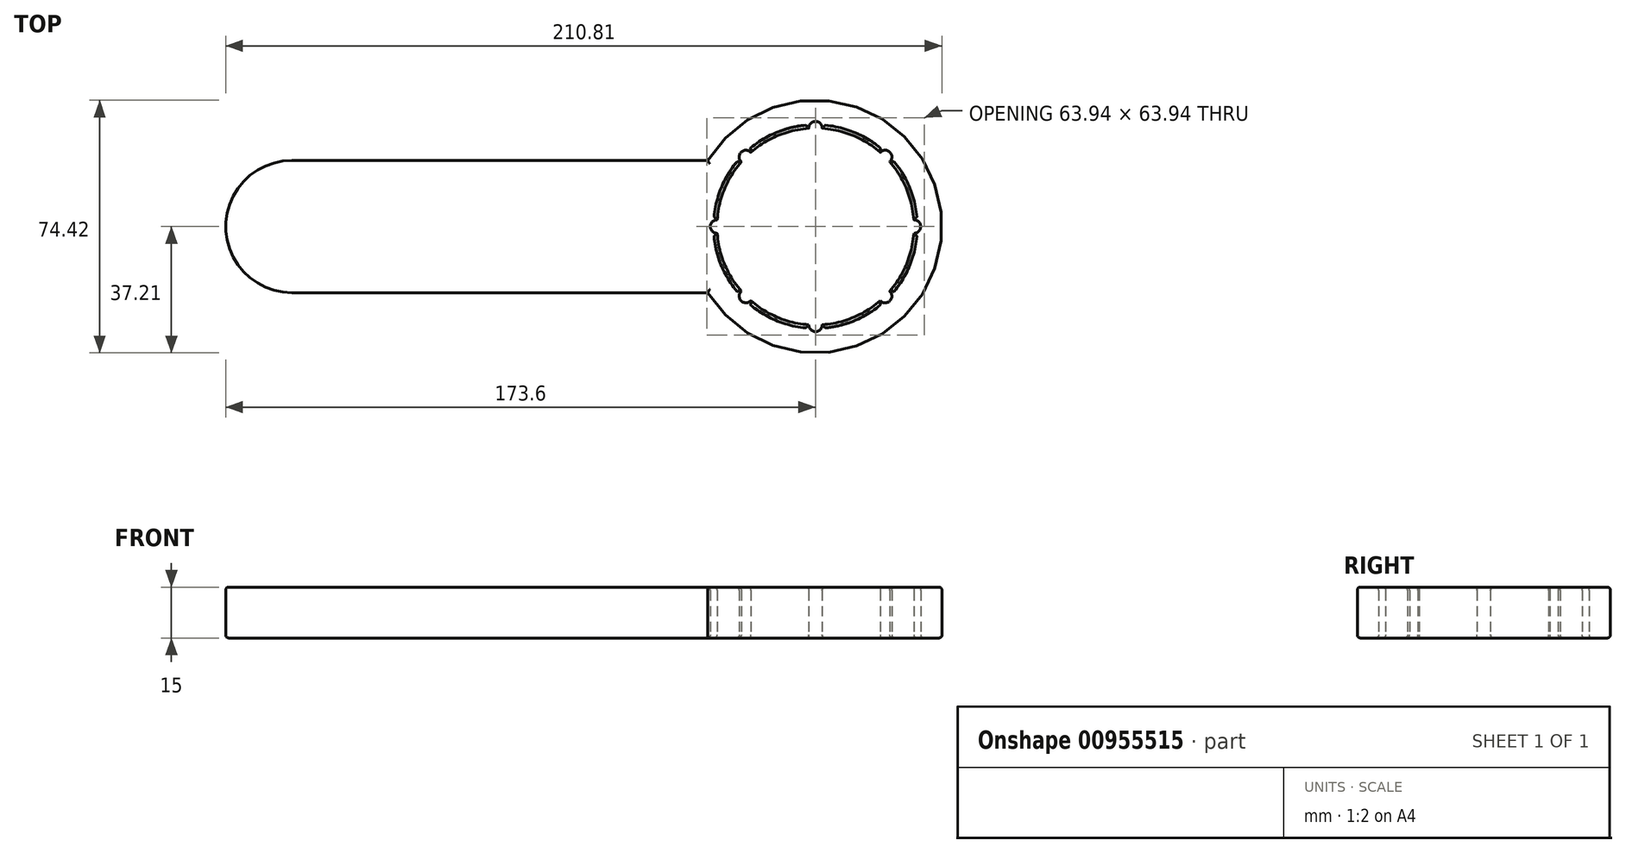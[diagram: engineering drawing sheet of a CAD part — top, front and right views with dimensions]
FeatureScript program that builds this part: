
annotation { "Feature Type Name" : "Feature", "Feature Type Description" : "" }
export const myFeature = defineFeature(function(context is Context, id is Id, definition is map)
    precondition{}
    {
        {
            var Q0;
            Q0=qCreatedBy(makeId("Top.planeOp"),FACE);
            var sketch = newSketch(context, id + "F0", { "sketchPlane" : qUnion([Q0])});
            skCircle(sketch, "E0", {"center": v(0, 0) * mm, "radius": 37.21 * mm});
            skArc(sketch, "E1", {"start": v(-20.5, 20.5) * mm, "mid": v(-26.4, 12) * mm, "end": v(-28.93, 1.95) * mm});
            skPoint(sketch, "E2", {"position": v(0, 29) * mm});
            skPoint(sketch, "E3", {"position": v(0, -29) * mm});
            skLineSegment(sketch, "E4.bottom", {"start": v(-31.72, 19.47) * mm, "end": v(-154.13, 19.47) * mm});
            skLineSegment(sketch, "E4.top", {"start": v(-3.98, -19.47) * mm, "end": v(-154.13, -19.47) * mm});
            skLineSegment(sketch, "E4.left", {"start": v(-3.98, 19.47) * mm, "end": v(-3.98, -19.47) * mm});
            skLineSegment(sketch, "E4.right", {"start": v(-154.13, 19.47) * mm, "end": v(-154.13, -19.47) * mm});
            skArc(sketch, "E5", {"start": v(-154.13, 19.47) * mm, "mid": v(-173.6, 0) * mm, "end": v(-154.13, -19.47) * mm});
            skArc(sketch, "E6.trimOffspring", {"start": v(-29, 0) * mm, "mid": v(-27.15, -10.2) * mm, "end": v(-21.84, -19.08) * mm});
            skArc(sketch, "E7.trimOffspring", {"start": v(-20.5, -20.5) * mm, "mid": v(-12, -26.4) * mm, "end": v(-1.95, -28.93) * mm});
            skArc(sketch, "E8.trimOffspring", {"start": v(0, -29) * mm, "mid": v(10.2, -27.15) * mm, "end": v(19.08, -21.84) * mm});
            skArc(sketch, "E9.trimOffspring", {"start": v(20.5, -20.5) * mm, "mid": v(26.4, -12) * mm, "end": v(28.93, -1.95) * mm});
            skArc(sketch, "E10.trimOffspring", {"start": v(20.5, 20.5) * mm, "mid": v(12, 26.4) * mm, "end": v(1.95, 28.93) * mm});
            skArc(sketch, "E11.trimOffspring", {"start": v(0, 29) * mm, "mid": v(-10.2, 27.15) * mm, "end": v(-19.08, 21.84) * mm});
            skPoint(sketch, "E12", {"position": v(-1.95, 29) * mm});
            skPoint(sketch, "E13", {"position": v(-21.88, 19.13) * mm});
            skPoint(sketch, "E14", {"position": v(-29, -1.95) * mm});
            skPoint(sketch, "E15", {"position": v(-19.13, -21.88) * mm});
            skPoint(sketch, "E16", {"position": v(1.95, -29) * mm});
            skPoint(sketch, "E17", {"position": v(21.88, -19.13) * mm});
            skPoint(sketch, "E18", {"position": v(29, 1.95) * mm});
            skPoint(sketch, "E19", {"position": v(19.13, 21.88) * mm});
            skCircle(sketch, "E20", {"center": v(0, 29) * mm, "radius": 1.97 * mm});
            skCircle(sketch, "E21.1.0", {"center": v(-20.5, 20.5) * mm, "radius": 1.97 * mm});
            skCircle(sketch, "E21.2.0", {"center": v(-29, 0) * mm, "radius": 1.97 * mm});
            skCircle(sketch, "E22.1.3.0", {"center": v(-20.5, -20.5) * mm, "radius": 1.97 * mm});
            skCircle(sketch, "E22.1.4.0", {"center": v(0, -29) * mm, "radius": 1.97 * mm});
            skCircle(sketch, "E22.1.5.0", {"center": v(20.5, -20.5) * mm, "radius": 1.97 * mm});
            skCircle(sketch, "E22.1.6.0", {"center": v(29, 0) * mm, "radius": 1.97 * mm});
            skCircle(sketch, "E22.1.7.0", {"center": v(20.5, 20.5) * mm, "radius": 1.97 * mm});
            skArc(sketch, "E22.2.7.0", {"start": v(29, 0) * mm, "mid": v(27.15, 10.2) * mm, "end": v(21.84, 19.08) * mm});
            skSolve(sketch);
        }
        {
            var Q0;
            Q0 = qSketchRegion(id + "F0", true);
            extrude(context, id + "F1", {"entities" : qUnion([Q0]), "depth" : 15 * mm, "offsetDistance" : 25 * mm});
        }
        {
            var Q0;
            Q0=makeQuery(id+"F1.opExtrude","CAP_FACE",FACE,{"disambiguationData":[OSD([sQuery(id+"F0.wireOp",EDGE,"E0"),sQuery(id+"F0.wireOp",EDGE,"E4.bottom"),sQuery(id+"F0.wireOp",EDGE,"E4.top"),sQuery(id+"F0.wireOp",EDGE,"E4.left"),sQuery(id+"F0.wireOp",EDGE,"E5"),sQuery(id+"F0.wireOp",EDGE,"E10.trimOffspring"),sQuery(id+"F0.wireOp",EDGE,"E20"),sQuery(id+"F0.wireOp",EDGE,"E21.1.0"),sQuery(id+"F0.wireOp",EDGE,"E11.trimOffspring"),sQuery(id+"F0.wireOp",EDGE,"E21.2.0"),sQuery(id+"F0.wireOp",EDGE,"E1"),sQuery(id+"F0.wireOp",EDGE,"E22.1.3.0"),sQuery(id+"F0.wireOp",EDGE,"E6.trimOffspring"),sQuery(id+"F0.wireOp",EDGE,"E22.1.4.0"),sQuery(id+"F0.wireOp",EDGE,"E7.trimOffspring"),sQuery(id+"F0.wireOp",EDGE,"E22.1.5.0"),sQuery(id+"F0.wireOp",EDGE,"E8.trimOffspring"),sQuery(id+"F0.wireOp",EDGE,"E22.1.6.0"),sQuery(id+"F0.wireOp",EDGE,"E9.trimOffspring"),sQuery(id+"F0.wireOp",EDGE,"E22.1.7.0"),sQuery(id+"F0.wireOp",EDGE,"E22.2.7.0")])],"isStart":false});
            fillet(context, id + "F2", {"entities" : qUnion([Q0]), "radius" : 1 * mm, "tangentPropagation" : true, "rho" : 0.5, "crossSection" : FilletCrossSection.CONIC, "allowEdgeOverflow" : false});
        }
        {
            var Q0;
            Q0=makeQuery(id+"F1.opExtrude","CAP_FACE",FACE,{"disambiguationData":[OSD([sQuery(id+"F0.wireOp",EDGE,"E0"),sQuery(id+"F0.wireOp",EDGE,"E4.bottom"),sQuery(id+"F0.wireOp",EDGE,"E4.top"),sQuery(id+"F0.wireOp",EDGE,"E5"),sQuery(id+"F0.wireOp",EDGE,"E10.trimOffspring"),sQuery(id+"F0.wireOp",EDGE,"E20"),sQuery(id+"F0.wireOp",EDGE,"E21.1.0"),sQuery(id+"F0.wireOp",EDGE,"E11.trimOffspring"),sQuery(id+"F0.wireOp",EDGE,"E21.2.0"),sQuery(id+"F0.wireOp",EDGE,"E1"),sQuery(id+"F0.wireOp",EDGE,"E22.1.3.0"),sQuery(id+"F0.wireOp",EDGE,"E6.trimOffspring"),sQuery(id+"F0.wireOp",EDGE,"E22.1.4.0"),sQuery(id+"F0.wireOp",EDGE,"E7.trimOffspring"),sQuery(id+"F0.wireOp",EDGE,"E22.1.5.0"),sQuery(id+"F0.wireOp",EDGE,"E8.trimOffspring"),sQuery(id+"F0.wireOp",EDGE,"E22.1.6.0"),sQuery(id+"F0.wireOp",EDGE,"E9.trimOffspring"),sQuery(id+"F0.wireOp",EDGE,"E22.1.7.0"),sQuery(id+"F0.wireOp",EDGE,"E22.2.7.0")])],"isStart":true});
            fillet(context, id + "F3", {"entities" : qUnion([Q0]), "radius" : 1 * mm, "tangentPropagation" : true, "rho" : 0.5, "crossSection" : FilletCrossSection.CONIC, "allowEdgeOverflow" : false});
        }
    });
